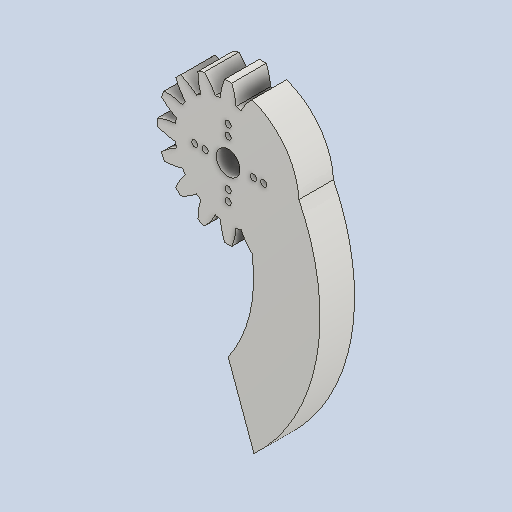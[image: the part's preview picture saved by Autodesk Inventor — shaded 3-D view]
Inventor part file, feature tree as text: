
AUTODESK INVENTOR PART (.ipt)
format: ipt  version: 2024 (Build 280153000, 153)  size: 238,080 bytes
history: native  units: in
note: dims shown in document units (in); Inventor stores cm internally (conversion verified against a paired STEP export)
features: other x13, sketch x4, plane x2
ambient origin geometry x8: Origin, YZ Plane, XZ Plane, XY Plane, X Axis, Y Axis, Z Axis, Center Point
bodies: Solid1 (feature_tree)
feature tree (19):
  other  "Spur Gear2"
  other  "Solid1::Spur Gear2"
  other  "TaggingFeature1"
  sketch  "Sketch1"  dims[d0=0.3937in]
  sketch  "Sketch2"  dims[d16=0.9213in]
  sketch  "Sketch3"  dims[d17=0.0in]
  sketch  "Sketch4"  dims[d41=0.0in d43=0.9213in d46=0.9213in d47=0.0in d48=0.0in]
  plane  "XZ Plane_1"
  plane  "Work Plane2"
  other  "Z Axis_1"
  other  "Srf1"
  other  "Srf1::Derived"
  other  "Distance iMate"
  other  "Align iMate"
  other  "Mesh iMate"
  other  "Axis iMate"
  other  "Position iMate"
  other  "Mesh iMate2"
  other  "Start plane iMate"
